# Revit family: Haworth_Tube Top_Light
name_source: partatom
category: Lighting Fixtures
revit_build: Autodesk Revit 2018 (Build: 20170223_1515(x64)
units: mm (PartAtom-declared; Revit-internal decimal feet)

## family parameters
Always vertical = Yes
Cut with Voids When Loaded = No
Light Source = Yes
OmniClass Number = 23.80.70.11.14
OmniClass Title = General Luminaries, Directional
Part Type = Normal
Room Calculation Point = No
Round Connector Dimension = Use Diameter
Shared = No
Work Plane-Based = No

## types (4) — shared parameters
Assembly Code = D5020200
Base Finish = Haworth _ Paint _ Collection White
Base Radius Bottom = 1 49/64"
Color Filter = 16777215
Dimming Lamp Color Temperature Shift = <None>
Emit Shape Visible in Rendering = No
Emit from Circle Diameter = 12"
Glass Finish = Haworth _ Glass _ Clear
Manufacturer = Haworth
Model = HCPL-TT
Photometric Web File = generic
Revision Number = 1
Size = Verify Final Dim. w/ Haworth
Tilt Angle = 90.00°
URL = http://www.haworth.com
URL - Product = https://www.haworth.com
Warranty = http://www.haworth.com
Wattage Comments = 6-13W 120V 60Hz

## per-type parameters (varying)
| type | Actual Depth | Actual Height | Actual Width | Base Radius to Center Bottom | Base Radius to Center Top | Base to Center Bottom | Description | Floor Lamp | Inside Radius Bottom | Large Table Lamp | Medium Table Lamp | Outside Radius Bottom | Small Table Lamp | Top Height |
| HCPL-TTF1 - Floor Light | 9" | 60" | 18" | 4 15/64" | 3 45/64" | 6" | Haworth Tube Top Floor Light | Yes | 1 75/256" | No | No | 1 49/64" | No | 12" |
| HCPL-TTT1 - Small Table Light | 4 1/2" | 14" | 9 1/2" | 1 25/64" | 1 77/128" | 2 1/4" | Haworth Tube Top Small Table Light | No | 5/8" | No | No | 55/64" | Yes | 6" |
| HCPL-TTT2 - Medium Table Light | 6 1/2" | 21" | 15" | 2 53/256" | 2 1/2" | 3 1/2" | Haworth Tube Top Medium Table Light | No | 251/256" | No | Yes | 1 75/256" | No | 9" |
| HCPL-TTT3 - Large Table Light | 9" | 27" | 18" | 3 19/256" | 3 1/4" | 4 1/4" | Haworth Tube Top Large Table Light | No | 1 145/256" | Yes | No | 1 45/256" | No | 12" |

## geometry (parser evidence)
native form markers: Sweep x2
no freeform markers — native parametric forms only
